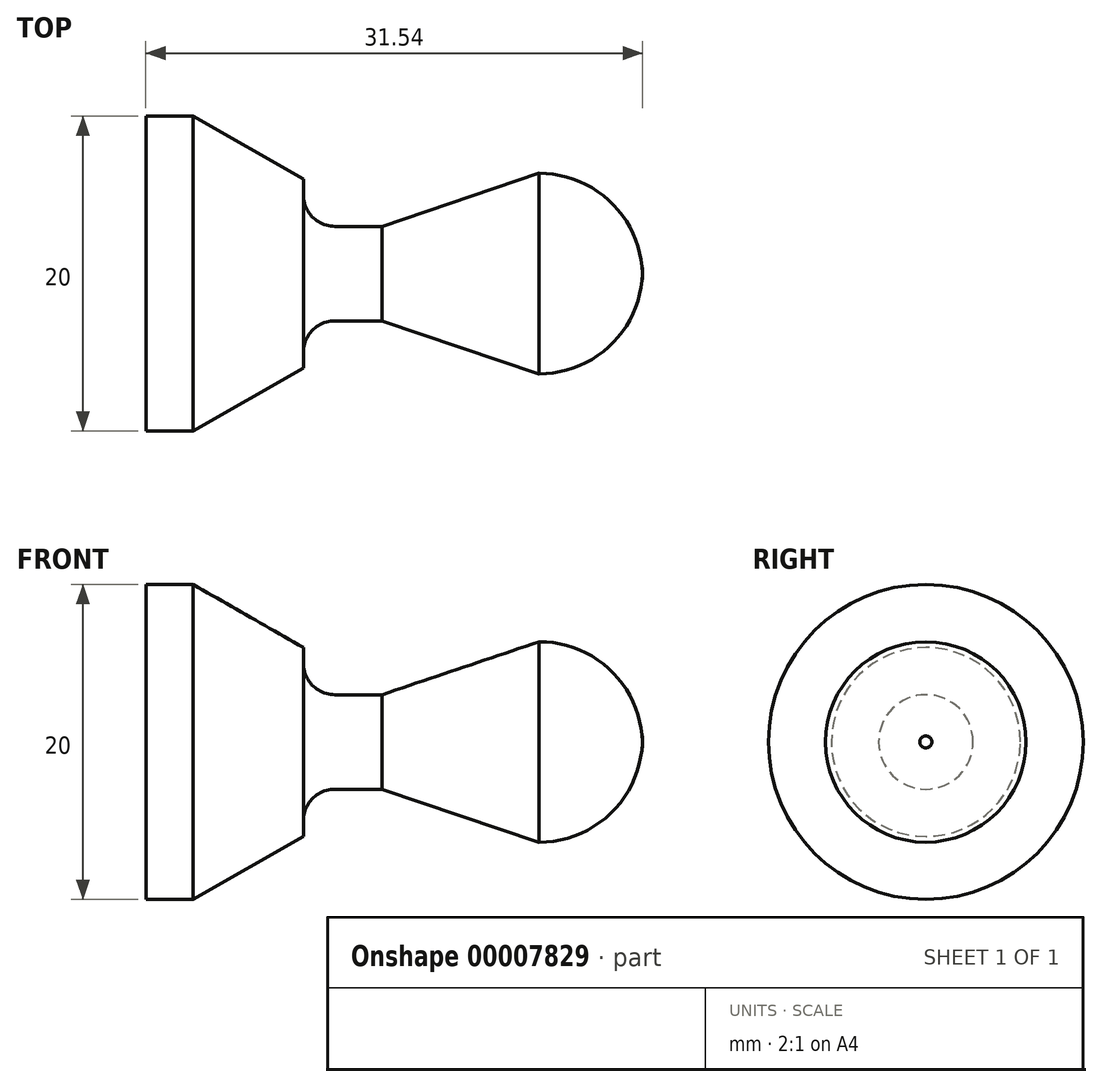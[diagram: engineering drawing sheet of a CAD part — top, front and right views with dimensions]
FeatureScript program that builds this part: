
annotation { "Feature Type Name" : "Feature", "Feature Type Description" : "" }
export const myFeature = defineFeature(function(context is Context, id is Id, definition is map)
    precondition{}
    {
        {
            var Q0;
            Q0=qCreatedBy(makeId("Front.planeOp"),FACE);
            var sketch = newSketch(context, id + "F0", { "sketchPlane" : qUnion([Q0])});
            skLineSegment(sketch, "E0", {"start": v(-16.43, 0) * mm, "end": v(20.98, 0) * mm});
            skArc(sketch, "E1", {"start": v(8.96, -6.37) * mm, "mid": v(13.53, -4.51) * mm, "end": v(15.51, 0) * mm});
            skLineSegment(sketch, "E2", {"start": v(8.96, -6.37) * mm, "end": v(-1.02, -3) * mm});
            skLineSegment(sketch, "E3", {"start": v(-1.02, -3) * mm, "end": v(-6.02, -3) * mm});
            skLineSegment(sketch, "E4", {"start": v(-6.02, -3) * mm, "end": v(-6.02, -6) * mm});
            skLineSegment(sketch, "E5", {"start": v(-6.02, -6) * mm, "end": v(-13.02, -10) * mm});
            skLineSegment(sketch, "E6", {"start": v(-13.02, -10) * mm, "end": v(-16.02, -10) * mm});
            skLineSegment(sketch, "E7", {"start": v(-16.02, -10) * mm, "end": v(-16.02, 0) * mm});
            skSolve(sketch);
        }
        {
            var Q0;
            {var subQ0=sQuery(id+"F0.wireOp",EDGE,"E1");Q0=makeQuery(id+"F0.imprint","IMPRINT",FACE,{"disambiguationData":[TD([[makeQuery(id+"F0.imprint","IMPRINT",EDGE,{"derivedFrom":subQ0}),1.0]])]});}
            var Q1;
            Q1=sQuery(id+"F0.wireOp",EDGE,"E0");
            revolve(context, id + "F1", {"entities" : qUnion([Q0]), "axis" : qUnion([Q1]), "revolveType" : RevolveType.FULL});
        }
        {
            var Q0;
            Q0=makeQuery(id+"F1.opRevolve","SWEPT_EDGE",EDGE,{"disambiguationData":[OSD([sQuery(id+"F0.wireOp",EDGE,"E3"),sQuery(id+"F0.wireOp",EDGE,"E4")])]});
            fillet(context, id + "F2", {"entities" : qUnion([Q0]), "radius" : 2 * mm, "allowEdgeOverflow" : false});
        }
    });
